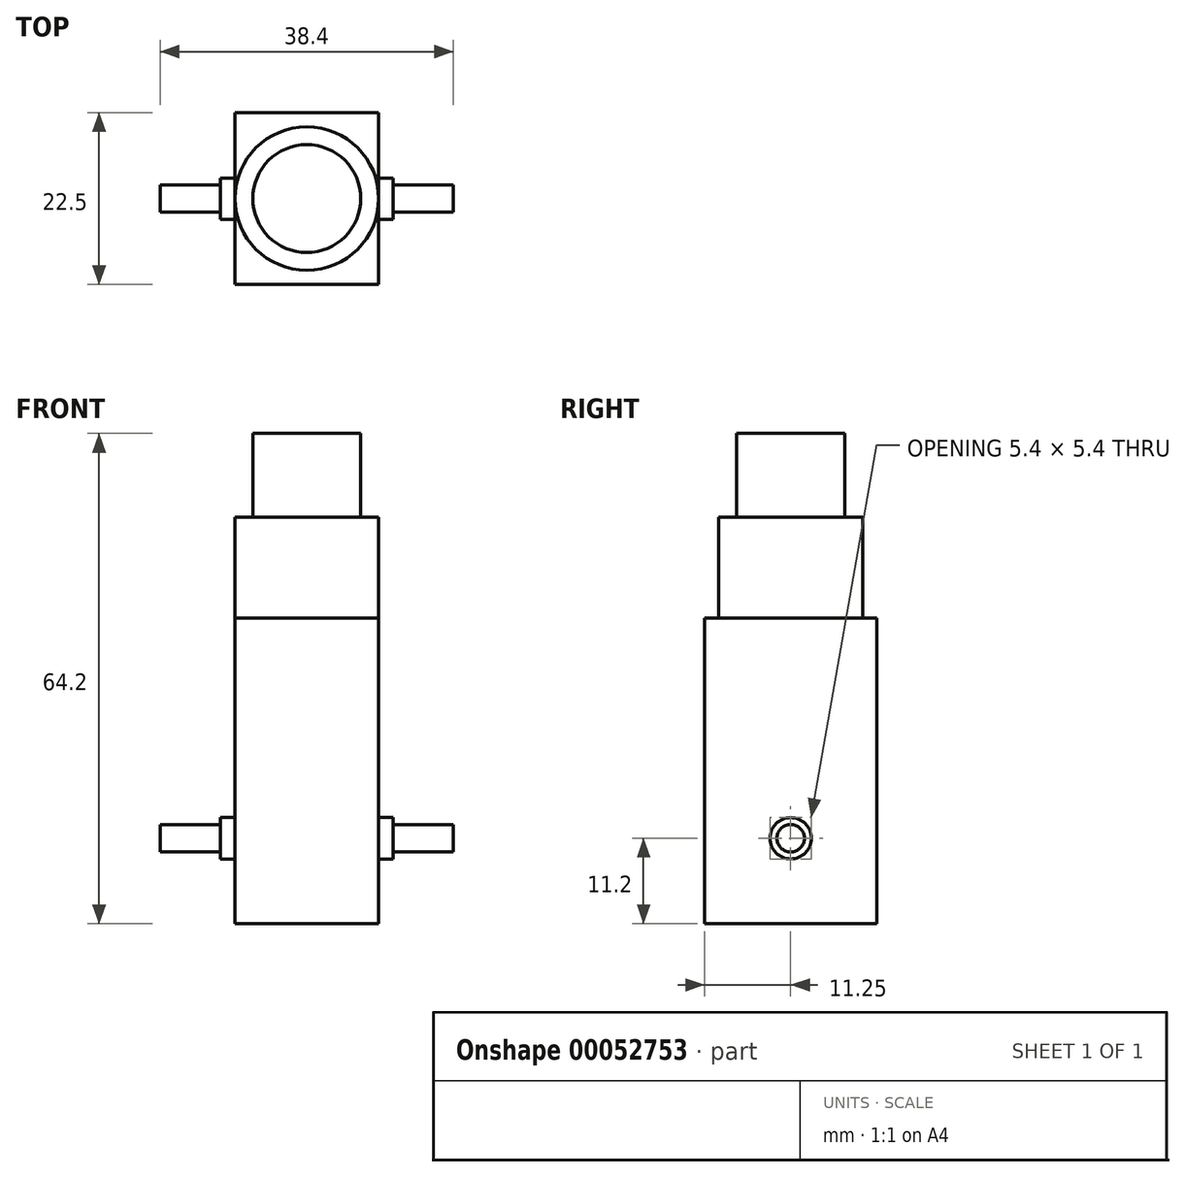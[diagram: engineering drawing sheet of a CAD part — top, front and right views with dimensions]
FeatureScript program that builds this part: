
annotation { "Feature Type Name" : "Feature", "Feature Type Description" : "" }
export const myFeature = defineFeature(function(context is Context, id is Id, definition is map)
    precondition{}
    {
        {
            var Q0;
            Q0=qCreatedBy(makeId("Top.planeOp"),FACE);
            var sketch = newSketch(context, id + "F0", { "sketchPlane" : qUnion([Q0])});
            skLineSegment(sketch, "E0.bottom", {"start": v(-9.4, 11.25) * mm, "end": v(9.4, 11.25) * mm});
            skLineSegment(sketch, "E0.top", {"start": v(-9.4, -11.25) * mm, "end": v(9.4, -11.25) * mm});
            skLineSegment(sketch, "E0.left", {"start": v(-9.4, 11.25) * mm, "end": v(-9.4, -11.25) * mm});
            skLineSegment(sketch, "E0.right", {"start": v(9.4, 11.25) * mm, "end": v(9.4, -11.25) * mm});
            skLineSegment(sketch, "E1", {"start": v(-9.4, 11.25) * mm, "end": v(9.4, -11.25) * mm, "construction": true});
            skSolve(sketch);
        }
        {
            var Q0;
            Q0 = qSketchRegion(id + "F0", true);
            extrude(context, id + "F1", {"entities" : qUnion([Q0]), "depth" : 40 * mm});
        }
        {
            var Q0;
            Q0=qCreatedBy(makeId("Front.planeOp"),FACE);
            var sketch = newSketch(context, id + "F2", { "sketchPlane" : qUnion([Q0])});
            skLineSegment(sketch, "E2", {"start": v(0, 64.2) * mm, "end": v(0, 40) * mm});
            skLineSegment(sketch, "E3", {"start": v(0, 40) * mm, "end": v(9.4, 40) * mm});
            skLineSegment(sketch, "E4", {"start": v(9.4, 40) * mm, "end": v(9.4, 53.23) * mm});
            skLineSegment(sketch, "E5", {"start": v(9.4, 53.23) * mm, "end": v(7.06, 53.23) * mm});
            skLineSegment(sketch, "E6", {"start": v(7.06, 53.23) * mm, "end": v(7.06, 64.2) * mm});
            skLineSegment(sketch, "E7", {"start": v(7.06, 64.2) * mm, "end": v(0, 64.2) * mm});
            skSolve(sketch);
        }
        {
            var Q0;
            Q0 = qSketchRegion(id + "F2", true);
            var Q1;
            Q1=sQuery(id+"F2.wireOp",EDGE,"E2");
            revolve(context, id + "F3", {"operationType" : NewBodyOperationType.ADD, "entities" : qUnion([Q0]), "axis" : qUnion([Q1]), "revolveType" : RevolveType.FULL});
        }
        {
            var Q0;
            Q0=qCreatedBy(makeId("Front.planeOp"),FACE);
            var sketch = newSketch(context, id + "F4", { "sketchPlane" : qUnion([Q0])});
            skLineSegment(sketch, "E8", {"start": v(9.4, 13.9) * mm, "end": v(11.3, 13.9) * mm});
            skLineSegment(sketch, "E9", {"start": v(11.3, 13.9) * mm, "end": v(11.3, 13) * mm});
            skLineSegment(sketch, "E10", {"start": v(11.3, 13) * mm, "end": v(19.2, 13) * mm});
            skLineSegment(sketch, "E11", {"start": v(19.2, 13) * mm, "end": v(19.2, 11.2) * mm});
            skLineSegment(sketch, "E12", {"start": v(19.2, 11.2) * mm, "end": v(9.4, 11.2) * mm});
            skLineSegment(sketch, "E13", {"start": v(9.4, 11.2) * mm, "end": v(9.4, 13.9) * mm});
            skLineSegment(sketch, "E14.MirrorCS", {"start": v(-9.4, 11.2) * mm, "end": v(-9.4, 13.9) * mm});
            skLineSegment(sketch, "E15.MirrorCS", {"start": v(-11.3, 13) * mm, "end": v(-19.2, 13) * mm});
            skLineSegment(sketch, "E16.MirrorCS", {"start": v(-19.2, 13) * mm, "end": v(-19.2, 11.2) * mm});
            skLineSegment(sketch, "E17.MirrorCS", {"start": v(-9.4, 13.9) * mm, "end": v(-11.3, 13.9) * mm});
            skLineSegment(sketch, "E18.MirrorCS", {"start": v(-19.2, 11.2) * mm, "end": v(-9.4, 11.2) * mm});
            skLineSegment(sketch, "E19.MirrorCS", {"start": v(-11.3, 13.9) * mm, "end": v(-11.3, 13) * mm});
            skLineSegment(sketch, "E20", {"start": v(-22.42, 11.2) * mm, "end": v(22.18, 11.2) * mm, "construction": true});
            skSolve(sketch);
        }
        {
            var Q0;
            Q0 = qSketchRegion(id + "F4", true);
            var Q1;
            Q1=sQuery(id+"F4.wireOp",EDGE,"E20");
            revolve(context, id + "F5", {"operationType" : NewBodyOperationType.ADD, "entities" : qUnion([Q0]), "axis" : qUnion([Q1]), "revolveType" : RevolveType.FULL});
        }
    });
